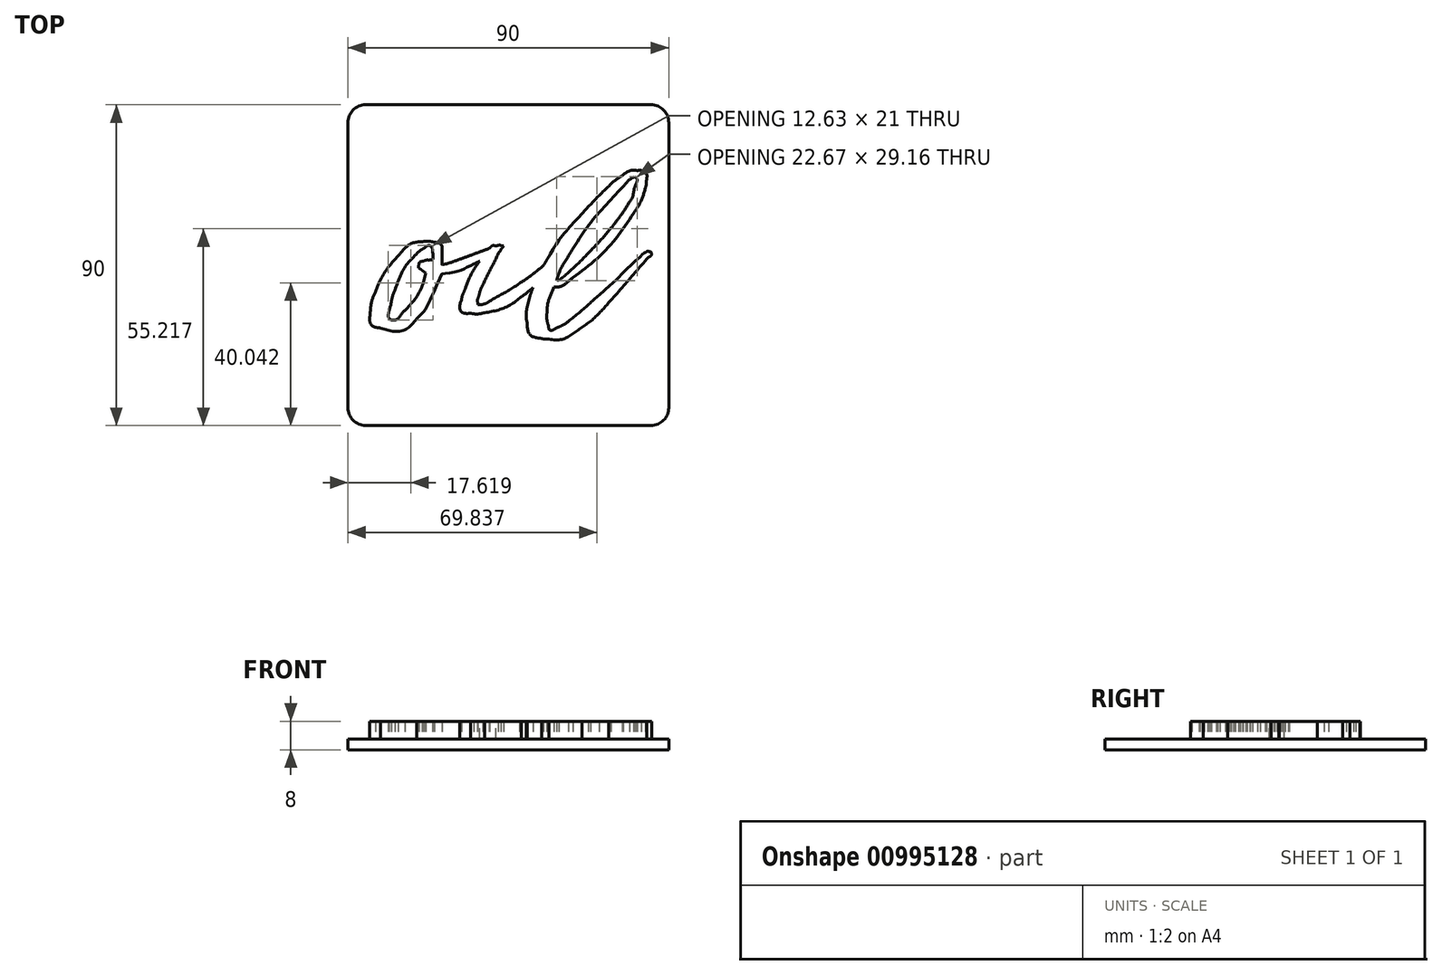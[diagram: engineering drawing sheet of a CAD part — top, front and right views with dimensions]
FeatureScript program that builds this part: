
annotation { "Feature Type Name" : "Feature", "Feature Type Description" : "" }
export const myFeature = defineFeature(function(context is Context, id is Id, definition is map)
    precondition{}
    {
        {
            var Q0;
            Q0=qCreatedBy(makeId("Top.planeOp"),FACE);
            var sketch = newSketch(context, id + "F0", { "sketchPlane" : qUnion([Q0])});
            skLineSegment(sketch, "E0.bottom", {"start": v(-46, 47.9) * mm, "end": v(44, 47.9) * mm});
            skLineSegment(sketch, "E0.top", {"start": v(-46, -42.1) * mm, "end": v(44, -42.1) * mm});
            skLineSegment(sketch, "E0.left", {"start": v(-46, 47.9) * mm, "end": v(-46, -42.1) * mm});
            skLineSegment(sketch, "E0.right", {"start": v(44, 47.9) * mm, "end": v(44, -42.1) * mm});
            skSolve(sketch);
        }
        {
            var Q0;
            Q0=makeQuery(id+"F0.imprint","IMPRINT",FACE,{"disambiguationData":[TD([[makeQuery(id+"F0.imprint","IMPRINT",EDGE,{"derivedFrom":sQuery(id+"F0.wireOp",EDGE,"E0.bottom")}),-1.0]])]});
            extrude(context, id + "F1", {"entities" : qUnion([Q0]), "oppositeDirection" : true, "depth" : 3 * mm, "offsetDistance" : 25 * mm});
        }
        {
            var Q0;
            Q0=makeQuery(id+"F1.opExtrude","SWEPT_EDGE",EDGE,{"disambiguationData":[OSD([sQuery(id+"F0.wireOp",EDGE,"E0.bottom"),sQuery(id+"F0.wireOp",EDGE,"E0.left")])]});
            var Q1;
            Q1=makeQuery(id+"F1.opExtrude","SWEPT_EDGE",EDGE,{"disambiguationData":[OSD([sQuery(id+"F0.wireOp",EDGE,"E0.bottom"),sQuery(id+"F0.wireOp",EDGE,"E0.right")])]});
            var Q2;
            Q2=makeQuery(id+"F1.opExtrude","SWEPT_EDGE",EDGE,{"disambiguationData":[OSD([sQuery(id+"F0.wireOp",EDGE,"E0.top"),sQuery(id+"F0.wireOp",EDGE,"E0.left")])]});
            var Q3;
            Q3=makeQuery(id+"F1.opExtrude","SWEPT_EDGE",EDGE,{"disambiguationData":[OSD([sQuery(id+"F0.wireOp",EDGE,"E0.top"),sQuery(id+"F0.wireOp",EDGE,"E0.right")])]});
            fillet(context, id + "F2", {"entities" : qUnion([Q0, Q1, Q2, Q3]), "radius" : 5 * mm, "tangentPropagation" : true, "allowEdgeOverflow" : false});
        }
        {
            var Q0;
            Q0=makeQuery(id+"F1.opExtrude","CAP_FACE",FACE,{"disambiguationData":[OSD([sQuery(id+"F0.wireOp",EDGE,"E0.bottom"),sQuery(id+"F0.wireOp",EDGE,"E0.top"),sQuery(id+"F0.wireOp",EDGE,"E0.left"),sQuery(id+"F0.wireOp",EDGE,"E0.right")])],"isStart":true});
            var sketch = newSketch(context, id + "F3", { "sketchPlane" : qUnion([Q0])});
            skFitSpline(sketch, "E1", {"points": [v(-0.87, 15.6) * mm, v(-0.87, 15.6) * mm, v(-0.87, 15.6) * mm, v(-0.76, 15.72) * mm, v(3.51, 20.43) * mm, v(3.53, 20.45) * mm, v(3.53, 20.46) * mm, v(3.9, 20.82) * mm, v(4.17, 21.28) * mm, v(4.44, 21.64) * mm]});
            skFitSpline(sketch, "E2", {"points": [v(4.44, 21.64) * mm, v(2.98, 22.47) * mm, v(2.89, 22.47) * mm, v(1.88, 22.1) * mm]});
            skFitSpline(sketch, "E3", {"points": [v(1.88, 22.1) * mm, v(1.1, 21.83) * mm, v(0.39, 21.44) * mm, v(-0.23, 20.94) * mm]});
            skFitSpline(sketch, "E4", {"points": [v(-0.23, 20.94) * mm, v(-0.85, 20.45) * mm, v(-1.38, 19.86) * mm, v(-1.8, 19.17) * mm]});
            skFitSpline(sketch, "E5", {"points": [v(-1.8, 19.17) * mm, v(-2.43, 18.07) * mm, v(-2.98, 16.88) * mm, v(-3.53, 15.78) * mm]});
            skFitSpline(sketch, "E6", {"points": [v(-3.53, 15.78) * mm, v(-3.72, 15.4) * mm, v(-3.62, 15.04) * mm, v(-3.72, 14.68) * mm]});
            skFitSpline(sketch, "E7", {"points": [v(-3.72, 14.68) * mm, v(-2.07, 14.4) * mm, v(-1.97, 14.5) * mm, v(-0.87, 15.6) * mm]});
            skFitSpline(sketch, "E8", {"points": [v(37.73, 6.6) * mm, v(37.18, 6.33) * mm, v(36.63, 5.96) * mm, v(36.26, 5.5) * mm]});
            skFitSpline(sketch, "E9", {"points": [v(36.26, 5.5) * mm, v(32.32, 1.84) * mm, v(28.47, -1.92) * mm, v(24.43, -5.5) * mm]});
            skFitSpline(sketch, "E10", {"points": [v(24.43, -5.5) * mm, v(21.68, -7.97) * mm, v(18.75, -10.54) * mm, v(15.81, -12.83) * mm]});
            skFitSpline(sketch, "E11", {"points": [v(15.81, -12.83) * mm, v(14.71, -13.75) * mm, v(13.34, -14.4) * mm, v(12.06, -15.03) * mm]});
            skFitSpline(sketch, "E12", {"points": [v(12.06, -15.03) * mm, v(11.14, -15.4) * mm, v(10.5, -15.22) * mm, v(10.31, -14.3) * mm]});
            skFitSpline(sketch, "E13", {"points": [v(10.31, -14.3) * mm, v(9.95, -13.02) * mm, v(9.76, -11.64) * mm, v(9.85, -10.45) * mm]});
            skFitSpline(sketch, "E14", {"points": [v(9.85, -10.45) * mm, v(10.04, -8.06) * mm, v(10.77, -5.68) * mm, v(11.78, -3.3) * mm]});
            skFitSpline(sketch, "E15", {"points": [v(11.78, -3.3) * mm, v(13.98, -3.02) * mm, v(15.54, -1.92) * mm, v(17.1, -0.64) * mm]});
            skFitSpline(sketch, "E16", {"points": [v(17.1, -0.64) * mm, v(23.7, 4.59) * mm, v(29.38, 10.64) * mm, v(34.15, 17.52) * mm]});
            skFitSpline(sketch, "E17", {"points": [v(34.15, 17.52) * mm, v(35.62, 19.72) * mm, v(36.72, 22.1) * mm, v(37.45, 24.58) * mm]});
            skFitSpline(sketch, "E18", {"points": [v(37.45, 24.58) * mm, v(37.64, 25.22) * mm, v(37.73, 25.95) * mm, v(37.73, 26.6) * mm]});
            skFitSpline(sketch, "E19", {"points": [v(37.73, 26.6) * mm, v(37.82, 28.43) * mm, v(36.9, 29.35) * mm, v(35.07, 29.44) * mm]});
            skFitSpline(sketch, "E20", {"points": [v(35.07, 29.44) * mm, v(33.6, 29.53) * mm, v(32.41, 29.07) * mm, v(31.22, 28.25) * mm]});
            skFitSpline(sketch, "E21", {"points": [v(31.22, 28.25) * mm, v(30.03, 27.42) * mm, v(28.83, 26.6) * mm, v(27.83, 25.68) * mm]});
            skFitSpline(sketch, "E22", {"points": [v(27.83, 25.68) * mm, v(25.63, 23.57) * mm, v(23.52, 21.46) * mm, v(21.5, 19.35) * mm]});
            skFitSpline(sketch, "E23", {"points": [v(21.5, 19.35) * mm, v(17.46, 14.95) * mm, v(13.52, 10.37) * mm, v(10.4, 5.32) * mm]});
            skFitSpline(sketch, "E24", {"points": [v(10.4, 5.32) * mm, v(9.89, 4.5) * mm, v(9.4, 3.67) * mm, v(8.92, 2.83) * mm]});
            skFitSpline(sketch, "E25", {"points": [v(8.92, 2.83) * mm, v(6.74, 1.05) * mm, v(4.49, -0.66) * mm, v(2.15, -2.2) * mm]});
            skFitSpline(sketch, "E26", {"points": [v(2.15, -2.2) * mm, v(-0.6, -4.03) * mm, v(-3.44, -5.59) * mm, v(-6.28, -7.24) * mm]});
            skFitSpline(sketch, "E27", {"points": [v(-6.28, -7.24) * mm, v(-7.2, -7.79) * mm, v(-8.3, -8.16) * mm, v(-9.58, -8.25) * mm]});
            skFitSpline(sketch, "E28", {"points": [v(-9.58, -8.25) * mm, v(-9.58, -7.6) * mm, v(-9.68, -7.06) * mm, v(-9.58, -6.6) * mm]});
            skFitSpline(sketch, "E29", {"points": [v(-9.58, -6.6) * mm, v(-9.13, -5.22) * mm, v(-8.76, -3.85) * mm, v(-8.12, -2.56) * mm]});
            skFitSpline(sketch, "E30", {"points": [v(-8.12, -2.56) * mm, v(-6.74, 0.37) * mm, v(-5.18, 3.3) * mm, v(-3.8, 6.15) * mm]});
            skFitSpline(sketch, "E31", {"points": [v(-3.8, 6.15) * mm, v(-3.56, 6.58) * mm, v(-3.2, 6.93) * mm, v(-3.09, 7.33) * mm]});
            skFitSpline(sketch, "E32", {"points": [v(-3.09, 7.33) * mm, v(-2.8, 7.6) * mm, v(-2.59, 7.9) * mm, v(-2.34, 8.26) * mm]});
            skFitSpline(sketch, "E33", {"points": [v(-2.34, 8.26) * mm, v(-2.9, 8.35) * mm, v(-3.44, 8.53) * mm, v(-3.8, 8.44) * mm]});
            skFitSpline(sketch, "E34", {"points": [v(-3.8, 8.44) * mm, v(-4.02, 8.4) * mm, v(-4.23, 8.34) * mm, v(-4.44, 8.28) * mm]});
            skFitSpline(sketch, "E35", {"points": [v(-4.44, 8.28) * mm, v(-5.25, 8.4) * mm, v(-5.68, 8.24) * mm, v(-6.3, 7.58) * mm]});
            skFitSpline(sketch, "E36", {"points": [v(-6.3, 7.58) * mm, v(-8.12, 6.94) * mm, v(-9.9, 6.28) * mm, v(-11.7, 5.62) * mm]});
            skFitSpline(sketch, "E37", {"points": [v(-11.7, 5.62) * mm, v(-13.47, 4.97) * mm, v(-15.24, 4.3) * mm, v(-17.01, 3.67) * mm]});
            skFitSpline(sketch, "E38", {"points": [v(-17.01, 3.67) * mm, v(-17.83, 3.4) * mm, v(-18.66, 3.21) * mm, v(-19.57, 3.03) * mm, v(-19.58, 3.03) * mm, v(-19.58, 3.04) * mm, v(-19.58, 6.6) * mm, v(-19.58, 6.6) * mm, v(-19.58, 6.61) * mm, v(-19.58, 8.08) * mm, v(-20.4, 9.08) * mm, v(-21.78, 9.36) * mm]});
            skFitSpline(sketch, "E39", {"points": [v(-21.78, 9.36) * mm, v(-22.88, 9.54) * mm, v(-24.07, 9.63) * mm, v(-25.17, 9.45) * mm]});
            skFitSpline(sketch, "E40", {"points": [v(-25.17, 9.45) * mm, v(-27.92, 9.08) * mm, v(-30.12, 7.52) * mm, v(-31.87, 5.5) * mm]});
            skFitSpline(sketch, "E41", {"points": [v(-31.87, 5.5) * mm, v(-34.52, 2.48) * mm, v(-36.73, -0.91) * mm, v(-38.28, -4.58) * mm]});
            skFitSpline(sketch, "E42", {"points": [v(-38.28, -4.58) * mm, v(-39.1, -6.6) * mm, v(-39.57, -8.61) * mm, v(-39.75, -10.81) * mm]});
            skFitSpline(sketch, "E43", {"points": [v(-39.75, -10.81) * mm, v(-39.84, -12.74) * mm, v(-39.2, -14.12) * mm, v(-36.82, -14.76) * mm]});
            skFitSpline(sketch, "E44", {"points": [v(-36.82, -14.76) * mm, v(-33.06, -15.67) * mm, v(-29.57, -15.03) * mm, v(-26.73, -12.2) * mm]});
            skFitSpline(sketch, "E45", {"points": [v(-26.73, -12.2) * mm, v(-24.9, -10.36) * mm, v(-23.52, -8.16) * mm, v(-22.42, -5.78) * mm, v(-22.42, -5.77) * mm, v(-22.42, -5.77) * mm, v(-19.67, 0.46) * mm, v(-19.67, 0.46) * mm, v(-19.67, 0.46) * mm, v(-16.55, 0.83) * mm, v(-13.52, 1.84) * mm, v(-10.68, 3.21) * mm]});
            skFitSpline(sketch, "E46", {"points": [v(-10.68, 3.21) * mm, v(-10.1, 3.5) * mm, v(-9.57, 3.75) * mm, v(-9.08, 3.99) * mm]});
            skFitSpline(sketch, "E47", {"points": [v(-9.08, 3.99) * mm, v(-10.66, 1.67) * mm, v(-11.97, -0.81) * mm, v(-12.98, -3.39) * mm]});
            skFitSpline(sketch, "E48", {"points": [v(-12.98, -3.39) * mm, v(-13.43, -4.58) * mm, v(-13.9, -5.68) * mm, v(-14.17, -6.87) * mm]});
            skFitSpline(sketch, "E49", {"points": [v(-14.17, -6.87) * mm, v(-14.63, -9.16) * mm, v(-13.8, -10.45) * mm, v(-11.5, -10.63) * mm]});
            skFitSpline(sketch, "E50", {"points": [v(-11.5, -10.63) * mm, v(-10.23, -10.81) * mm, v(-8.85, -10.72) * mm, v(-7.66, -10.45) * mm]});
            skFitSpline(sketch, "E51", {"points": [v(-7.66, -10.45) * mm, v(-3.9, -9.71) * mm, v(-0.41, -8.25) * mm, v(2.7, -5.96) * mm]});
            skFitSpline(sketch, "E52", {"points": [v(2.7, -5.96) * mm, v(3.82, -5.15) * mm, v(4.9, -4.3) * mm, v(5.94, -3.4) * mm]});
            skFitSpline(sketch, "E53", {"points": [v(5.94, -3.4) * mm, v(5.47, -4.62) * mm, v(5.06, -5.87) * mm, v(4.72, -7.15) * mm]});
            skFitSpline(sketch, "E54", {"points": [v(4.72, -7.15) * mm, v(4.26, -9.07) * mm, v(3.99, -11.18) * mm, v(4.26, -13.2) * mm]});
            skFitSpline(sketch, "E55", {"points": [v(4.26, -13.2) * mm, v(4.63, -15.86) * mm, v(5.82, -17.14) * mm, v(8.39, -17.7) * mm]});
            skFitSpline(sketch, "E56", {"points": [v(8.39, -17.7) * mm, v(9.03, -17.87) * mm, v(9.76, -17.87) * mm, v(10.4, -17.87) * mm]});
            skFitSpline(sketch, "E57", {"points": [v(10.4, -17.87) * mm, v(13.98, -17.97) * mm, v(16.91, -16.5) * mm, v(19.67, -14.57) * mm]});
            skFitSpline(sketch, "E58", {"points": [v(19.67, -14.57) * mm, v(22.42, -12.56) * mm, v(24.9, -10.17) * mm, v(27.18, -7.6) * mm]});
            skFitSpline(sketch, "E59", {"points": [v(27.18, -7.6) * mm, v(30.76, -3.57) * mm, v(34.24, 0.46) * mm, v(37.82, 4.59) * mm]});
            skFitSpline(sketch, "E60", {"points": [v(37.82, 4.59) * mm, v(38.37, 5.14) * mm, v(39.1, 5.6) * mm, v(39.01, 6.7) * mm]});
            skFitSpline(sketch, "E61", {"points": [v(39.01, 6.7) * mm, v(38.55, 6.7) * mm, v(38, 6.8) * mm, v(37.73, 6.6) * mm]});
            skFitSpline(sketch, "E62", {"points": [v(-24.8, 4.04) * mm, v(-25.36, 3.95) * mm, v(-25.9, 3.67) * mm, v(-26.09, 2.94) * mm]});
            skFitSpline(sketch, "E63", {"points": [v(-26.09, 2.94) * mm, v(-26.18, 2.2) * mm, v(-25.72, 1.84) * mm, v(-25.17, 1.47) * mm]});
            skFitSpline(sketch, "E64", {"points": [v(-25.17, 1.47) * mm, v(-24.9, 1.2) * mm, v(-24.62, 1.01) * mm, v(-24.16, 0.74) * mm]});
            skFitSpline(sketch, "E65", {"points": [v(-24.16, 0.74) * mm, v(-25.26, -3.2) * mm, v(-27.28, -6.78) * mm, v(-30.03, -9.8) * mm]});
            skFitSpline(sketch, "E66", {"points": [v(-30.03, -9.8) * mm, v(-31.13, -11) * mm, v(-32.14, -12.28) * mm, v(-33.8, -12.56) * mm]});
            skFitSpline(sketch, "E67", {"points": [v(-33.8, -12.56) * mm, v(-34.62, -11.73) * mm, v(-34.62, -10.72) * mm, v(-34.43, -9.8) * mm]});
            skFitSpline(sketch, "E68", {"points": [v(-34.43, -9.8) * mm, v(-33.88, -7.88) * mm, v(-33.52, -5.96) * mm, v(-32.78, -4.12) * mm]});
            skFitSpline(sketch, "E69", {"points": [v(-32.78, -4.12) * mm, v(-31.5, -0.64) * mm, v(-29.76, 2.66) * mm, v(-27.28, 5.5) * mm]});
            skFitSpline(sketch, "E70", {"points": [v(-27.28, 5.5) * mm, v(-26.46, 6.33) * mm, v(-25.45, 7.16) * mm, v(-24.44, 7.8) * mm]});
            skFitSpline(sketch, "E71", {"points": [v(-24.44, 7.8) * mm, v(-23.34, 8.44) * mm, v(-22.51, 7.98) * mm, v(-22.24, 6.7) * mm]});
            skFitSpline(sketch, "E72", {"points": [v(-22.24, 6.7) * mm, v(-22.15, 6.06) * mm, v(-22.15, 5.41) * mm, v(-22.05, 4.5) * mm]});
            skFitSpline(sketch, "E73", {"points": [v(-22.05, 4.5) * mm, v(-23.15, 4.31) * mm, v(-23.98, 4.31) * mm, v(-24.8, 4.04) * mm]});
            skFitSpline(sketch, "E74", {"points": [v(31.04, 24.76) * mm, v(32.04, 25.95) * mm, v(33.05, 26.96) * mm, v(34.43, 27.7) * mm]});
            skFitSpline(sketch, "E75", {"points": [v(34.43, 27.7) * mm, v(35.16, 26.96) * mm, v(35.07, 26.32) * mm, v(34.8, 25.59) * mm]});
            skFitSpline(sketch, "E76", {"points": [v(34.8, 25.59) * mm, v(34.24, 23.94) * mm, v(33.88, 22.1) * mm, v(32.96, 20.64) * mm]});
            skFitSpline(sketch, "E77", {"points": [v(32.96, 20.64) * mm, v(31.59, 18.34) * mm, v(30.03, 16.14) * mm, v(28.38, 14.03) * mm]});
            skFitSpline(sketch, "E78", {"points": [v(28.38, 14.03) * mm, v(26.36, 11.56) * mm, v(24.25, 9.2) * mm, v(22.06, 6.92) * mm]});
            skFitSpline(sketch, "E79", {"points": [v(22.06, 6.92) * mm, v(19.87, 4.64) * mm, v(17.6, 2.43) * mm, v(15.26, 0.28) * mm]});
            skFitSpline(sketch, "E80", {"points": [v(15.26, 0.28) * mm, v(14.62, -0.27) * mm, v(13.98, -0.73) * mm, v(13.25, -1.28) * mm]});
            skFitSpline(sketch, "E81", {"points": [v(13.25, -1.28) * mm, v(13.16, -1.37) * mm, v(12.97, -1.28) * mm, v(12.51, -1.46) * mm]});
            skFitSpline(sketch, "E82", {"points": [v(12.51, -1.46) * mm, v(13.8, 2.02) * mm, v(15.54, 4.96) * mm, v(17.37, 7.9) * mm]});
            skFitSpline(sketch, "E83", {"points": [v(17.37, 7.9) * mm, v(21.4, 13.94) * mm, v(26.08, 19.44) * mm, v(31.04, 24.76) * mm]});
            skSolve(sketch);
        }
        {
            var Q0;
            Q0=makeQuery(id+"F3.imprint","IMPRINT",FACE,{"disambiguationData":[TD([[makeQuery(id+"F3.imprint","IMPRINT",EDGE,{"derivedFrom":sQuery(id+"F3.wireOp",EDGE,"E8")}),1.0]])]});
            extrude(context, id + "F4", {"entities" : qUnion([Q0]), "depth" : 5 * mm, "offsetDistance" : 25 * mm});
        }
    });
